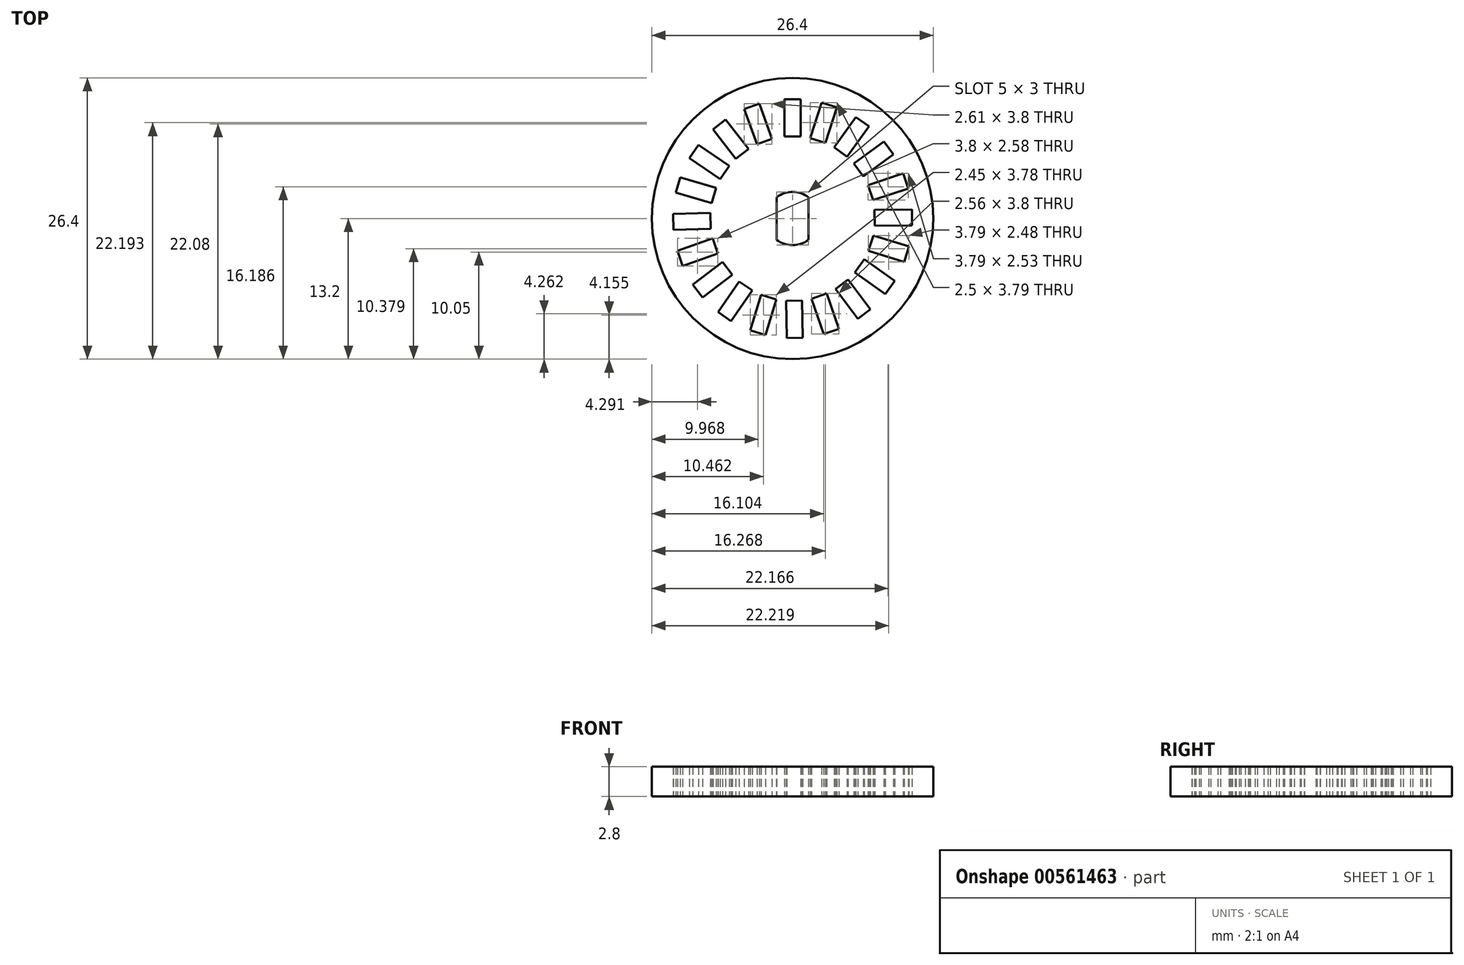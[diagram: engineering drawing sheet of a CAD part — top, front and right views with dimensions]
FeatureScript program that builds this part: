
annotation { "Feature Type Name" : "Feature", "Feature Type Description" : "" }
export const myFeature = defineFeature(function(context is Context, id is Id, definition is map)
    precondition{}
    {
        {
            var Q0;
            Q0=qCreatedBy(makeId("Top.planeOp"),FACE);
            var sketch = newSketch(context, id + "F0", { "sketchPlane" : qUnion([Q0])});
            skCircle(sketch, "E0", {"center": v(0, 0) * mm, "radius": 13.2 * mm});
            skLineSegment(sketch, "E1.bottom", {"start": v(-0.75, 11.2) * mm, "end": v(0.75, 11.2) * mm});
            skLineSegment(sketch, "E1.top", {"start": v(-0.75, 7.7) * mm, "end": v(0.75, 7.7) * mm});
            skLineSegment(sketch, "E1.left", {"start": v(-0.75, 11.2) * mm, "end": v(-0.75, 7.7) * mm});
            skLineSegment(sketch, "E1.right", {"start": v(0.75, 11.2) * mm, "end": v(0.75, 7.7) * mm});
            skLineSegment(sketch, "E2.1.0", {"start": v(4.16, 10.43) * mm, "end": v(3.08, 7.1) * mm});
            skLineSegment(sketch, "E2.1.1", {"start": v(2.73, 10.89) * mm, "end": v(4.16, 10.43) * mm});
            skLineSegment(sketch, "E2.1.2", {"start": v(2.73, 10.89) * mm, "end": v(1.65, 7.56) * mm});
            skLineSegment(sketch, "E2.1.3", {"start": v(1.65, 7.56) * mm, "end": v(3.08, 7.1) * mm});
            skLineSegment(sketch, "E2.2.0", {"start": v(7.16, 8.65) * mm, "end": v(5.11, 5.8) * mm});
            skLineSegment(sketch, "E2.2.1", {"start": v(5.94, 9.52) * mm, "end": v(7.16, 8.65) * mm});
            skLineSegment(sketch, "E2.2.2", {"start": v(5.94, 9.52) * mm, "end": v(3.9, 6.68) * mm});
            skLineSegment(sketch, "E2.2.3", {"start": v(3.9, 6.68) * mm, "end": v(5.11, 5.8) * mm});
            skLineSegment(sketch, "E2.3.0", {"start": v(9.47, 6.03) * mm, "end": v(6.65, 3.96) * mm});
            skLineSegment(sketch, "E2.3.1", {"start": v(8.58, 7.24) * mm, "end": v(9.47, 6.03) * mm});
            skLineSegment(sketch, "E2.3.2", {"start": v(8.58, 7.24) * mm, "end": v(5.76, 5.16) * mm});
            skLineSegment(sketch, "E2.3.3", {"start": v(5.76, 5.16) * mm, "end": v(6.65, 3.96) * mm});
            skLineSegment(sketch, "E2.4.0", {"start": v(10.86, 2.83) * mm, "end": v(7.54, 1.72) * mm});
            skLineSegment(sketch, "E2.4.1", {"start": v(10.39, 4.25) * mm, "end": v(10.86, 2.83) * mm});
            skLineSegment(sketch, "E2.4.2", {"start": v(10.39, 4.25) * mm, "end": v(7.07, 3.14) * mm});
            skLineSegment(sketch, "E2.4.3", {"start": v(7.07, 3.14) * mm, "end": v(7.54, 1.72) * mm});
            skLineSegment(sketch, "E2.5.0", {"start": v(11.2, -0.65) * mm, "end": v(7.7, -0.68) * mm});
            skLineSegment(sketch, "E2.5.1", {"start": v(11.2, 0.85) * mm, "end": v(11.2, -0.65) * mm});
            skLineSegment(sketch, "E2.5.2", {"start": v(11.2, 0.85) * mm, "end": v(7.7, 0.82) * mm});
            skLineSegment(sketch, "E2.5.3", {"start": v(7.7, 0.82) * mm, "end": v(7.7, -0.68) * mm});
            skLineSegment(sketch, "E2.6.0", {"start": v(10.47, -4.06) * mm, "end": v(7.13, -3.01) * mm});
            skLineSegment(sketch, "E2.6.1", {"start": v(10.91, -2.63) * mm, "end": v(10.47, -4.06) * mm});
            skLineSegment(sketch, "E2.6.2", {"start": v(10.91, -2.63) * mm, "end": v(7.57, -1.58) * mm});
            skLineSegment(sketch, "E2.6.3", {"start": v(7.57, -1.58) * mm, "end": v(7.13, -3.01) * mm});
            skLineSegment(sketch, "E2.7.0", {"start": v(8.71, -7.08) * mm, "end": v(5.85, -5.06) * mm});
            skLineSegment(sketch, "E2.7.1", {"start": v(9.58, -5.85) * mm, "end": v(8.71, -7.08) * mm});
            skLineSegment(sketch, "E2.7.2", {"start": v(9.58, -5.85) * mm, "end": v(6.72, -3.83) * mm});
            skLineSegment(sketch, "E2.7.3", {"start": v(6.72, -3.83) * mm, "end": v(5.85, -5.06) * mm});
            skLineSegment(sketch, "E2.8.0", {"start": v(6.12, -9.41) * mm, "end": v(4.02, -6.61) * mm});
            skLineSegment(sketch, "E2.8.1", {"start": v(7.32, -8.51) * mm, "end": v(6.12, -9.41) * mm});
            skLineSegment(sketch, "E2.8.2", {"start": v(7.32, -8.51) * mm, "end": v(5.22, -5.71) * mm});
            skLineSegment(sketch, "E2.8.3", {"start": v(5.22, -5.71) * mm, "end": v(4.02, -6.61) * mm});
            skLineSegment(sketch, "E2.9.0", {"start": v(2.93, -10.84) * mm, "end": v(1.8, -7.53) * mm});
            skLineSegment(sketch, "E2.9.1", {"start": v(4.35, -10.35) * mm, "end": v(2.93, -10.84) * mm});
            skLineSegment(sketch, "E2.9.2", {"start": v(4.35, -10.35) * mm, "end": v(3.2, -7.04) * mm});
            skLineSegment(sketch, "E2.9.3", {"start": v(3.2, -7.04) * mm, "end": v(1.8, -7.53) * mm});
            skLineSegment(sketch, "E2.10.0", {"start": v(-0.54, -11.21) * mm, "end": v(-0.6, -7.71) * mm});
            skLineSegment(sketch, "E2.10.1", {"start": v(0.96, -11.18) * mm, "end": v(-0.54, -11.21) * mm});
            skLineSegment(sketch, "E2.10.2", {"start": v(0.96, -11.18) * mm, "end": v(0.9, -7.68) * mm});
            skLineSegment(sketch, "E2.10.3", {"start": v(0.9, -7.68) * mm, "end": v(-0.6, -7.71) * mm});
            skLineSegment(sketch, "E2.11.0", {"start": v(-3.96, -10.5) * mm, "end": v(-2.95, -7.15) * mm});
            skLineSegment(sketch, "E2.11.1", {"start": v(-2.53, -10.94) * mm, "end": v(-3.96, -10.5) * mm});
            skLineSegment(sketch, "E2.11.2", {"start": v(-2.53, -10.94) * mm, "end": v(-1.51, -7.59) * mm});
            skLineSegment(sketch, "E2.11.3", {"start": v(-1.51, -7.59) * mm, "end": v(-2.95, -7.15) * mm});
            skLineSegment(sketch, "E2.12.0", {"start": v(-7, -8.78) * mm, "end": v(-5, -5.9) * mm});
            skLineSegment(sketch, "E2.12.1", {"start": v(-5.77, -9.63) * mm, "end": v(-7, -8.78) * mm});
            skLineSegment(sketch, "E2.12.2", {"start": v(-5.77, -9.63) * mm, "end": v(-3.77, -6.76) * mm});
            skLineSegment(sketch, "E2.12.3", {"start": v(-3.77, -6.76) * mm, "end": v(-5, -5.9) * mm});
            skLineSegment(sketch, "E2.13.0", {"start": v(-9.36, -6.2) * mm, "end": v(-6.57, -4.08) * mm});
            skLineSegment(sketch, "E2.13.1", {"start": v(-8.45, -7.4) * mm, "end": v(-9.36, -6.2) * mm});
            skLineSegment(sketch, "E2.13.2", {"start": v(-8.45, -7.4) * mm, "end": v(-5.66, -5.27) * mm});
            skLineSegment(sketch, "E2.13.3", {"start": v(-5.66, -5.27) * mm, "end": v(-6.57, -4.08) * mm});
            skLineSegment(sketch, "E2.14.0", {"start": v(-10.8, -3.03) * mm, "end": v(-7.5, -1.86) * mm});
            skLineSegment(sketch, "E2.14.1", {"start": v(-10.3, -4.44) * mm, "end": v(-10.8, -3.03) * mm});
            skLineSegment(sketch, "E2.14.2", {"start": v(-10.3, -4.44) * mm, "end": v(-7, -3.27) * mm});
            skLineSegment(sketch, "E2.14.3", {"start": v(-7, -3.27) * mm, "end": v(-7.5, -1.86) * mm});
            skLineSegment(sketch, "E2.15.0", {"start": v(-11.22, 0.44) * mm, "end": v(-7.72, 0.54) * mm});
            skLineSegment(sketch, "E2.15.1", {"start": v(-11.18, -1.06) * mm, "end": v(-11.22, 0.44) * mm});
            skLineSegment(sketch, "E2.15.2", {"start": v(-11.18, -1.06) * mm, "end": v(-7.68, -0.96) * mm});
            skLineSegment(sketch, "E2.15.3", {"start": v(-7.68, -0.96) * mm, "end": v(-7.72, 0.54) * mm});
            skLineSegment(sketch, "E2.16.0", {"start": v(-10.54, 3.87) * mm, "end": v(-7.18, 2.88) * mm});
            skLineSegment(sketch, "E2.16.1", {"start": v(-10.96, 2.43) * mm, "end": v(-10.54, 3.87) * mm});
            skLineSegment(sketch, "E2.16.2", {"start": v(-10.96, 2.43) * mm, "end": v(-7.6, 1.44) * mm});
            skLineSegment(sketch, "E2.16.3", {"start": v(-7.6, 1.44) * mm, "end": v(-7.18, 2.88) * mm});
            skLineSegment(sketch, "E2.17.0", {"start": v(-8.84, 6.92) * mm, "end": v(-5.95, 4.95) * mm});
            skLineSegment(sketch, "E2.17.1", {"start": v(-9.68, 5.68) * mm, "end": v(-8.84, 6.92) * mm});
            skLineSegment(sketch, "E2.17.2", {"start": v(-9.68, 5.68) * mm, "end": v(-6.79, 3.7) * mm});
            skLineSegment(sketch, "E2.17.3", {"start": v(-6.79, 3.7) * mm, "end": v(-5.95, 4.95) * mm});
            skLineSegment(sketch, "E2.18.0", {"start": v(-6.29, 9.3) * mm, "end": v(-4.14, 6.54) * mm});
            skLineSegment(sketch, "E2.18.1", {"start": v(-7.47, 8.38) * mm, "end": v(-6.29, 9.3) * mm});
            skLineSegment(sketch, "E2.18.2", {"start": v(-7.47, 8.38) * mm, "end": v(-5.32, 5.62) * mm});
            skLineSegment(sketch, "E2.18.3", {"start": v(-5.32, 5.62) * mm, "end": v(-4.14, 6.54) * mm});
            skLineSegment(sketch, "E2.19.0", {"start": v(-3.13, 10.78) * mm, "end": v(-1.93, 7.5) * mm});
            skLineSegment(sketch, "E2.19.1", {"start": v(-4.54, 10.27) * mm, "end": v(-3.13, 10.78) * mm});
            skLineSegment(sketch, "E2.19.2", {"start": v(-4.54, 10.27) * mm, "end": v(-3.34, 6.98) * mm});
            skLineSegment(sketch, "E2.19.3", {"start": v(-3.34, 6.98) * mm, "end": v(-1.93, 7.5) * mm});
            skLineSegment(sketch, "E2.anchor1", {"start": v(0, 0) * mm, "end": v(0.75, 7.7) * mm, "construction": true});
            skLineSegment(sketch, "E2.anchor2", {"start": v(0, 0) * mm, "end": v(-1.93, 7.5) * mm, "construction": true});
            skCircle(sketch, "E3", {"center": v(0, 0) * mm, "radius": 2.5 * mm});
            skLineSegment(sketch, "E4", {"start": v(-1.5, 2) * mm, "end": v(-1.5, -2) * mm});
            skLineSegment(sketch, "E5", {"start": v(1.5, 2) * mm, "end": v(1.5, -2) * mm});
            skSolve(sketch);
        }
        {
            var Q0;
            Q0=makeQuery(id+"F0.imprint","IMPRINT",FACE,{"disambiguationData":[TD([[makeQuery(id+"F0.imprint","IMPRINT",EDGE,{"derivedFrom":sQuery(id+"F0.wireOp",EDGE,"E0")}),1.0]])]});
            var Q1;
            {var subQ0=sQuery(id+"F0.wireOp",EDGE,"E4");Q1=makeQuery(id+"F0.imprint","IMPRINT",FACE,{"disambiguationData":[TD([[makeQuery(id+"F0.imprint","IMPRINT",EDGE,{"derivedFrom":subQ0}),-1.0]])]});}
            var Q2;
            {var subQ0=sQuery(id+"F0.wireOp",EDGE,"E5");Q2=makeQuery(id+"F0.imprint","IMPRINT",FACE,{"disambiguationData":[TD([[makeQuery(id+"F0.imprint","IMPRINT",EDGE,{"derivedFrom":subQ0}),1.0]])]});}
            extrude(context, id + "F1", {"entities" : qUnion([Q0, Q1, Q2]), "depth" : 2.8 * mm, "offsetDistance" : 25 * mm});
        }
    });
